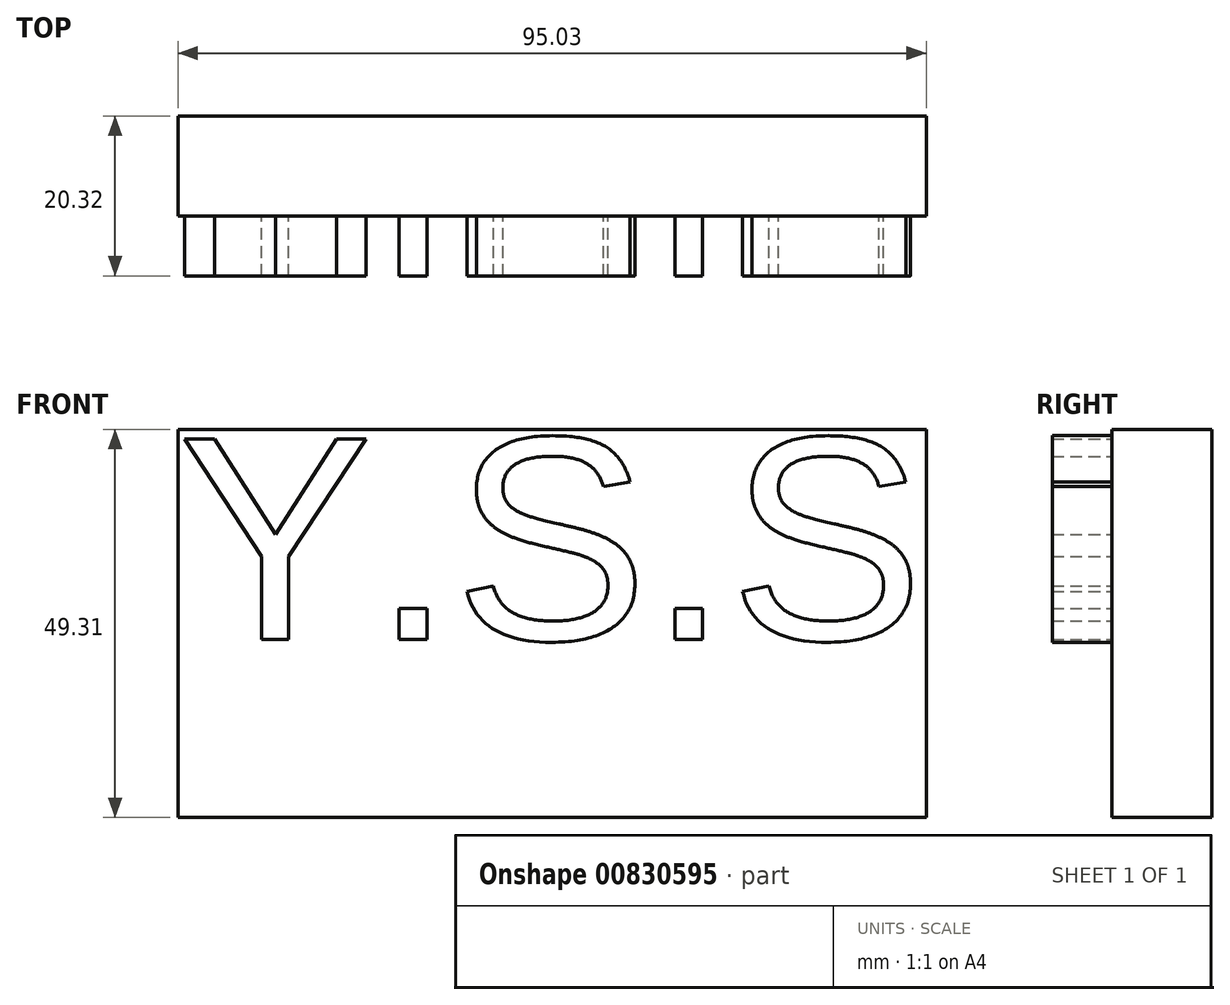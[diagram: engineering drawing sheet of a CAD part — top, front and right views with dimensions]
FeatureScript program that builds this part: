
annotation { "Feature Type Name" : "Feature", "Feature Type Description" : "" }
export const myFeature = defineFeature(function(context is Context, id is Id, definition is map)
    precondition{}
    {
        {
            var Q0;
            Q0=qCreatedBy(makeId("Front.planeOp"),FACE);
            var sketch = newSketch(context, id + "F0", { "sketchPlane" : qUnion([Q0])});
            skLineSegment(sketch, "E0.bottom", {"start": v(0, 0) * mm, "end": v(95.03, 0) * mm});
            skLineSegment(sketch, "E0.top", {"start": v(0, 49.31) * mm, "end": v(95.03, 49.31) * mm});
            skLineSegment(sketch, "E0.left", {"start": v(0, 0) * mm, "end": v(0, 49.31) * mm});
            skLineSegment(sketch, "E0.right", {"start": v(95.03, 0) * mm, "end": v(95.03, 49.31) * mm});
            skSolve(sketch);
        }
        {
            var Q0;
            Q0=makeQuery(id+"F0.imprint","IMPRINT",FACE,{"disambiguationData":[TD([[makeQuery(id+"F0.imprint","IMPRINT",EDGE,{"derivedFrom":sQuery(id+"F0.wireOp",EDGE,"E0.bottom")}),1.0]])]});
            extrude(context, id + "F1", {"entities" : qUnion([Q0]), "depth" : 12.7 * mm, "offsetDistance" : 25.4 * mm});
        }
        {
            var Q0;
            Q0=makeQuery(id+"F1.opExtrude","CAP_FACE",FACE,{"disambiguationData":[OSD([sQuery(id+"F0.wireOp",EDGE,"E0.bottom"),sQuery(id+"F0.wireOp",EDGE,"E0.top"),sQuery(id+"F0.wireOp",EDGE,"E0.left"),sQuery(id+"F0.wireOp",EDGE,"E0.right")])],"isStart":false});
            var sketch = newSketch(context, id + "F2", { "sketchPlane" : qUnion([Q0])});
            skText(sketch, "E1", { "text": "Y.S.S", "fontName": "Arimo-Regular.ttf"});
            const initialGuessF2  = {"E1": [0, 0.02263, 1, 0, 0.02668]};
            skSetInitialGuess(sketch, initialGuessF2);
            skSolve(sketch);
        }
        {
            var Q0;
            Q0=makeQuery(id+"F2.imprint","IMPRINT",FACE,{"disambiguationData":[TD([[makeQuery(id+"F2.imprint","IMPRINT",EDGE,{"derivedFrom":sQuery(id+"F2.wireOp",EDGE,"E1.sketch_text.stroke-0")}),-1.0]])]});
            var Q1;
            Q1 = qSketchRegion(id + "F2", true);
            extrude(context, id + "F3", {"entities" : qUnion([Q0, Q1]), "operationType" : NewBodyOperationType.ADD, "depth" : 7.62 * mm, "offsetDistance" : 25.4 * mm});
        }
    });
